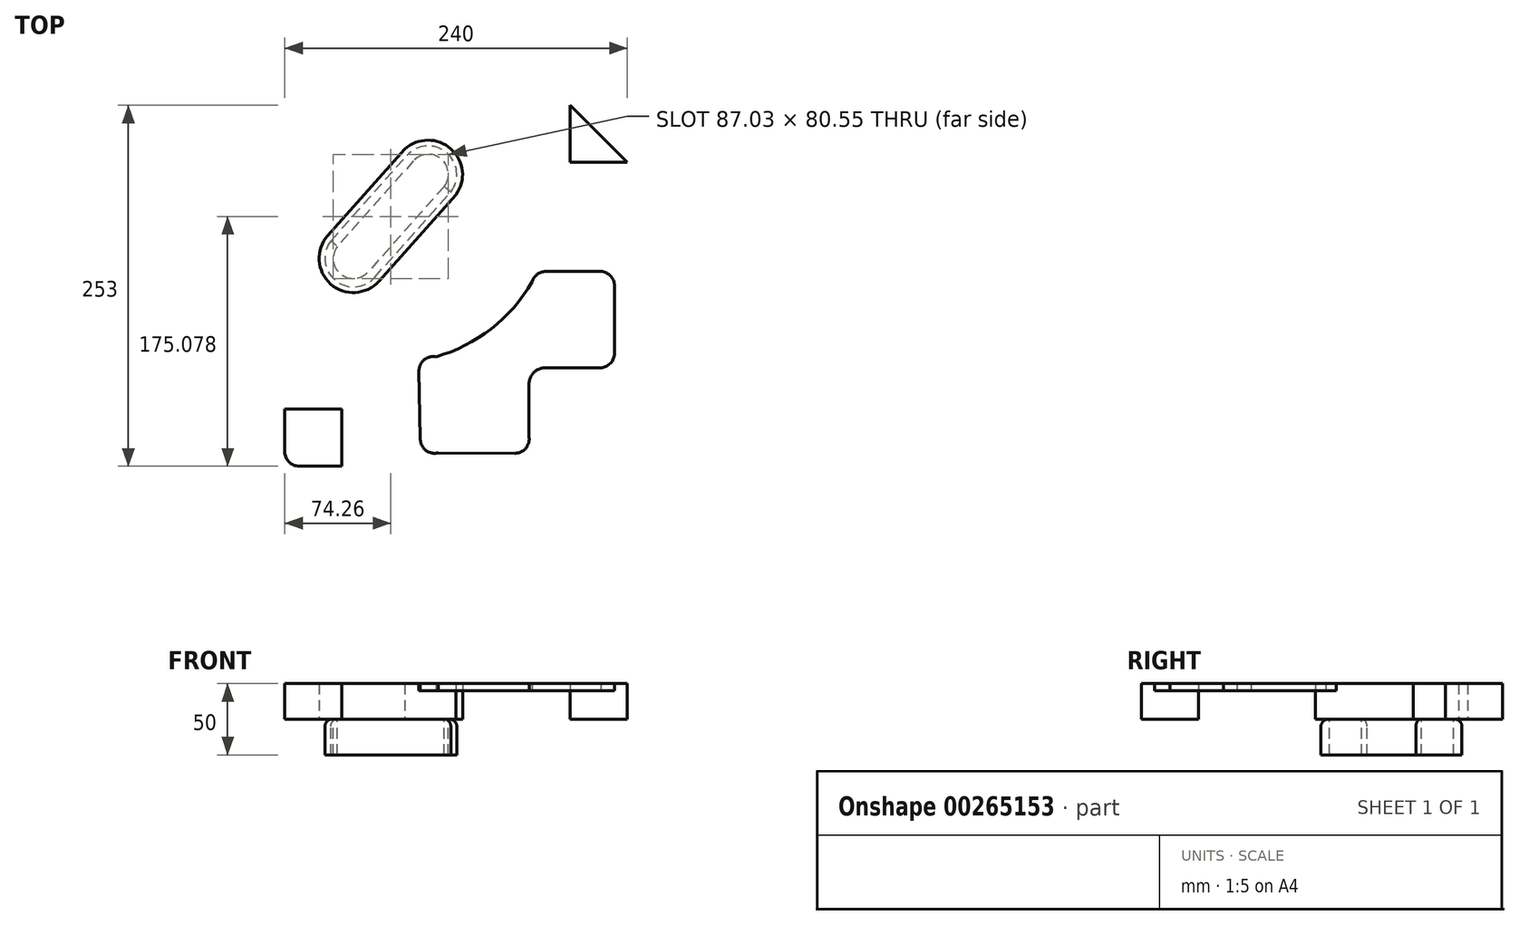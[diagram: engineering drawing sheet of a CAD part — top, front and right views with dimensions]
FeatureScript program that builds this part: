
annotation { "Feature Type Name" : "Feature", "Feature Type Description" : "" }
export const myFeature = defineFeature(function(context is Context, id is Id, definition is map)
    precondition{}
    {
        {
            var Q0;
            Q0=qCreatedBy(makeId("Top.planeOp"),FACE);
            var sketch = newSketch(context, id + "F0", { "sketchPlane" : qUnion([Q0])});
            skLineSegment(sketch, "E0.bottom", {"start": v(120, -126.5) * mm, "end": v(-120, -126.5) * mm});
            skLineSegment(sketch, "E0.top", {"start": v(120, 126.5) * mm, "end": v(-120, 126.5) * mm});
            skLineSegment(sketch, "E0.left", {"start": v(120, -126.5) * mm, "end": v(120, 126.5) * mm});
            skLineSegment(sketch, "E0.right", {"start": v(-120, -126.5) * mm, "end": v(-120, 126.5) * mm});
            skPoint(sketch, "E0.middle", {"position": v(0, 0) * mm});
            skLineSegment(sketch, "E1.bottom", {"start": v(120, 126.5) * mm, "end": v(80, 126.5) * mm});
            skLineSegment(sketch, "E1.top", {"start": v(120, 86.5) * mm, "end": v(80, 86.5) * mm});
            skLineSegment(sketch, "E1.left", {"start": v(120, 126.5) * mm, "end": v(120, 86.5) * mm});
            skLineSegment(sketch, "E1.right", {"start": v(80, 126.5) * mm, "end": v(80, 86.5) * mm});
            skLineSegment(sketch, "E2.bottom", {"start": v(-120, -126.5) * mm, "end": v(-80, -126.5) * mm});
            skLineSegment(sketch, "E2.top", {"start": v(-120, -86.5) * mm, "end": v(-80, -86.5) * mm});
            skLineSegment(sketch, "E2.left", {"start": v(-120, -126.5) * mm, "end": v(-120, -86.5) * mm});
            skLineSegment(sketch, "E2.right", {"start": v(-80, -126.5) * mm, "end": v(-80, -86.5) * mm});
            skLineSegment(sketch, "E3", {"start": v(80, 126.5) * mm, "end": v(120, 86.5) * mm});
            skLineSegment(sketch, "E4", {"start": v(-120, -86.5) * mm, "end": v(-80, -126.5) * mm});
            skLineSegment(sketch, "E5", {"start": v(111, 0) * mm, "end": v(111, -47.5) * mm});
            skArc(sketch, "E6", {"start": v(111, 0) * mm, "mid": v(108.27, 6.87) * mm, "end": v(101.57, 9.98) * mm});
            skArc(sketch, "E7", {"start": v(41.21, -117.5) * mm, "mid": v(48.64, -114.2) * mm, "end": v(51.16, -106.48) * mm});
            skArc(sketch, "E8", {"start": v(-25.06, -106.92) * mm, "mid": v(-21.43, -115.22) * mm, "end": v(-12.6, -117.19) * mm});
            skArc(sketch, "E9", {"start": v(-14.18, -49.84) * mm, "mid": v(-22.4, -51.99) * mm, "end": v(-26, -59.68) * mm});
            skLineSegment(sketch, "E10", {"start": v(101.57, 9.98) * mm, "end": v(62.86, 9.98) * mm});
            skArc(sketch, "E11", {"start": v(62.86, 9.98) * mm, "mid": v(56.82, 7.95) * mm, "end": v(53.23, 2.69) * mm});
            skArc(sketch, "E12", {"start": v(101.03, -57.5) * mm, "mid": v(108.08, -54.56) * mm, "end": v(111, -47.5) * mm});
            skLineSegment(sketch, "E13", {"start": v(-12.6, -117.19) * mm, "end": v(41.21, -117.5) * mm});
            skLineSegment(sketch, "E14", {"start": v(-25.06, -106.92) * mm, "end": v(-26, -59.68) * mm});
            skLineSegment(sketch, "E15", {"start": v(51.16, -106.48) * mm, "end": v(51.16, -69.28) * mm});
            skLineSegment(sketch, "E16", {"start": v(101.03, -57.5) * mm, "end": v(62.32, -57.62) * mm});
            skArc(sketch, "E17", {"start": v(62.32, -57.62) * mm, "mid": v(54.26, -61.07) * mm, "end": v(51.16, -69.28) * mm});
            skLineSegment(sketch, "E18", {"start": v(-87.77, 31.47) * mm, "end": v(-34.48, 91.28) * mm});
            skLineSegment(sketch, "E19", {"start": v(-57, 5.87) * mm, "end": v(-3.71, 65.68) * mm});
            skArc(sketch, "E20", {"start": v(-3.71, 65.68) * mm, "mid": v(-6.72, 93.35) * mm, "end": v(-34.48, 91.28) * mm});
            skArc(sketch, "E21", {"start": v(-87.77, 31.47) * mm, "mid": v(-84.76, 3.8) * mm, "end": v(-57, 5.87) * mm});
            skLineSegment(sketch, "E22", {"start": v(-8.33, 69.52) * mm, "end": v(-61.62, 9.71) * mm});
            skLineSegment(sketch, "E23", {"start": v(-29.86, 87.44) * mm, "end": v(-83.15, 27.63) * mm});
            skArc(sketch, "E24", {"start": v(-8.33, 69.52) * mm, "mid": v(-10.43, 88.9) * mm, "end": v(-29.86, 87.44) * mm});
            skArc(sketch, "E25", {"start": v(-83.15, 27.63) * mm, "mid": v(-81.05, 8.26) * mm, "end": v(-61.62, 9.71) * mm});
            skLineSegment(sketch, "E26", {"start": v(-35.84, 95.77) * mm, "end": v(-89.85, 35.15) * mm});
            skLineSegment(sketch, "E27", {"start": v(-54.02, 3.21) * mm, "end": v(0, 63.84) * mm});
            skArc(sketch, "E28", {"start": v(-89.85, 35.15) * mm, "mid": v(-87.9, 1.26) * mm, "end": v(-54.02, 3.21) * mm});
            skArc(sketch, "E29", {"start": v(0, 63.84) * mm, "mid": v(-3.55, 95.92) * mm, "end": v(-35.84, 95.77) * mm});
            skArc(sketch, "E30", {"start": v(-14.18, -49.84) * mm, "mid": v(24.68, -30.2) * mm, "end": v(53.23, 2.69) * mm});
            skSolve(sketch);
        }
        {
            var Q0;
            Q0=makeQuery(id+"F0.imprint","IMPRINT",FACE,{"disambiguationData":[TD([[makeQuery(id+"F0.imprint","IMPRINT",EDGE,{"derivedFrom":sQuery(id+"F0.wireOp",EDGE,"E2.top")}),-1.0]])]});
            var Q1;
            Q1=makeQuery(id+"F0.imprint","IMPRINT",FACE,{"disambiguationData":[TD([[makeQuery(id+"F0.imprint","IMPRINT",EDGE,{"derivedFrom":sQuery(id+"F0.wireOp",EDGE,"E1.top")}),-1.0]])]});
            var Q2;
            Q2=makeQuery(id+"F0.imprint","IMPRINT",FACE,{"disambiguationData":[TD([[makeQuery(id+"F0.imprint","IMPRINT",EDGE,{"derivedFrom":sQuery(id+"F0.wireOp",EDGE,"E0.bottom")}),-1.0]])]});
            var Q3;
            Q3=makeQuery(id+"F0.imprint","IMPRINT",FACE,{"disambiguationData":[TD([[makeQuery(id+"F0.imprint","IMPRINT",EDGE,{"derivedFrom":sQuery(id+"F0.wireOp",EDGE,"E18")}),1.0]])]});
            var Q4;
            Q4=makeQuery(id+"F0.imprint","IMPRINT",FACE,{"disambiguationData":[TD([[makeQuery(id+"F0.imprint","IMPRINT",EDGE,{"derivedFrom":sQuery(id+"F0.wireOp",EDGE,"E18")}),-1.0]])]});
            var Q5;
            Q5=makeQuery(id+"F0.imprint","IMPRINT",FACE,{"disambiguationData":[TD([[makeQuery(id+"F0.imprint","IMPRINT",EDGE,{"derivedFrom":sQuery(id+"F0.wireOp",EDGE,"E22")}),-1.0]])]});
            var Q6;
            Q6=makeQuery(id+"F0.imprint","IMPRINT",FACE,{"disambiguationData":[TD([[makeQuery(id+"F0.imprint","IMPRINT",EDGE,{"derivedFrom":sQuery(id+"F0.wireOp",EDGE,"E5")}),-1.0]])]});
            extrude(context, id + "F1", {"entities" : qUnion([Q0, Q1, Q2, Q3, Q4, Q5, Q6]), "depth" : 25 * mm});
        }
        {
            var Q0;
            Q0=makeQuery(id+"F1.opExtrude","SWEPT_EDGE",EDGE,{"disambiguationData":[OSD([sQuery(id+"F0.wireOp",EDGE,"E0.top"),sQuery(id+"F0.wireOp",EDGE,"E0.right")])]});
            var Q1;
            Q1=makeQuery(id+"F1.opExtrude","SWEPT_EDGE",EDGE,{"disambiguationData":[OSD([sQuery(id+"F0.wireOp",EDGE,"E0.bottom"),sQuery(id+"F0.wireOp",EDGE,"E0.left")])]});
            fillet(context, id + "F2", {"entities" : qUnion([Q0, Q1]), "radius" : 10 * mm, "tangentPropagation" : true, "allowEdgeOverflow" : false});
        }
        {
            var Q0;
            Q0=makeQuery(id+"F0.imprint","IMPRINT",FACE,{"disambiguationData":[TD([[makeQuery(id+"F0.imprint","IMPRINT",EDGE,{"derivedFrom":sQuery(id+"F0.wireOp",EDGE,"E18")}),-1.0]])]});
            extrude(context, id + "F3", {"entities" : qUnion([Q0]), "oppositeDirection" : true, "depth" : 25 * mm});
        }
        {
            var Q0;
            Q0=makeQuery(id+"F0.imprint","IMPRINT",FACE,{"disambiguationData":[TD([[makeQuery(id+"F0.imprint","IMPRINT",EDGE,{"derivedFrom":sQuery(id+"F0.wireOp",EDGE,"E5")}),-1.0]])]});
            extrude(context, id + "F4", {"entities" : qUnion([Q0]), "operationType" : NewBodyOperationType.REMOVE, "depth" : 20 * mm});
        }
        {
            var Q0;
            Q0=makeQuery(id+"F3.opExtrude","CAP_EDGE",EDGE,{"disambiguationData":[OSD([sQuery(id+"F0.wireOp",EDGE,"E19")])],"isStart":true});
            var Q1;
            Q1=makeQuery(id+"F3.opExtrude","CAP_EDGE",EDGE,{"disambiguationData":[OSD([sQuery(id+"F0.wireOp",EDGE,"E20")])],"isStart":true});
            var Q2;
            Q2=makeQuery(id+"F3.opExtrude","CAP_EDGE",EDGE,{"disambiguationData":[OSD([sQuery(id+"F0.wireOp",EDGE,"E18")])],"isStart":true});
            var Q3;
            Q3=makeQuery(id+"F3.opExtrude","CAP_EDGE",EDGE,{"disambiguationData":[OSD([sQuery(id+"F0.wireOp",EDGE,"E21")])],"isStart":true});
            var Q4;
            Q4=makeQuery(id+"F4.boolean.opBoolean","COPY",EDGE,{"derivedFrom":makeQuery(id+"F4.opExtrude","CAP_EDGE",EDGE,{"disambiguationData":[OSD([sQuery(id+"F0.wireOp",EDGE,"E30")])],"isStart":false})});
            var Q5;
            Q5=makeQuery(id+"F4.boolean.opBoolean","COPY",EDGE,{"derivedFrom":makeQuery(id+"F4.opExtrude","CAP_EDGE",EDGE,{"disambiguationData":[OSD([sQuery(id+"F0.wireOp",EDGE,"E14")])],"isStart":false})});
            var Q6;
            Q6=makeQuery(id+"F4.boolean.opBoolean","COPY",EDGE,{"derivedFrom":makeQuery(id+"F4.opExtrude","CAP_EDGE",EDGE,{"disambiguationData":[OSD([sQuery(id+"F0.wireOp",EDGE,"E9")])],"isStart":false})});
            var Q7;
            Q7=makeQuery(id+"F4.boolean.opBoolean","COPY",EDGE,{"derivedFrom":makeQuery(id+"F4.opExtrude","CAP_EDGE",EDGE,{"disambiguationData":[OSD([sQuery(id+"F0.wireOp",EDGE,"E11")])],"isStart":false})});
            var Q8;
            Q8=makeQuery(id+"F4.boolean.opBoolean","COPY",EDGE,{"derivedFrom":makeQuery(id+"F4.opExtrude","CAP_EDGE",EDGE,{"disambiguationData":[OSD([sQuery(id+"F0.wireOp",EDGE,"E8")])],"isStart":false})});
            var Q9;
            Q9=makeQuery(id+"F4.boolean.opBoolean","COPY",EDGE,{"derivedFrom":makeQuery(id+"F4.opExtrude","CAP_EDGE",EDGE,{"disambiguationData":[OSD([sQuery(id+"F0.wireOp",EDGE,"E10")])],"isStart":false})});
            var Q10;
            Q10=makeQuery(id+"F4.boolean.opBoolean","COPY",EDGE,{"derivedFrom":makeQuery(id+"F4.opExtrude","CAP_EDGE",EDGE,{"disambiguationData":[OSD([sQuery(id+"F0.wireOp",EDGE,"E13")])],"isStart":false})});
            var Q11;
            Q11=makeQuery(id+"F4.boolean.opBoolean","COPY",EDGE,{"derivedFrom":makeQuery(id+"F4.opExtrude","CAP_EDGE",EDGE,{"disambiguationData":[OSD([sQuery(id+"F0.wireOp",EDGE,"E7")])],"isStart":false})});
            var Q12;
            Q12=makeQuery(id+"F4.boolean.opBoolean","COPY",EDGE,{"derivedFrom":makeQuery(id+"F4.opExtrude","CAP_EDGE",EDGE,{"disambiguationData":[OSD([sQuery(id+"F0.wireOp",EDGE,"E15")])],"isStart":false})});
            var Q13;
            Q13=makeQuery(id+"F4.boolean.opBoolean","COPY",EDGE,{"derivedFrom":makeQuery(id+"F4.opExtrude","CAP_EDGE",EDGE,{"disambiguationData":[OSD([sQuery(id+"F0.wireOp",EDGE,"E16")])],"isStart":false})});
            fillet(context, id + "F5", {"entities" : qUnion([Q0, Q1, Q2, Q3, Q4, Q5, Q6, Q7, Q8, Q9, Q10, Q11, Q12, Q13]), "radius" : 5 * mm, "tangentPropagation" : true, "allowEdgeOverflow" : false});
        }
    });
